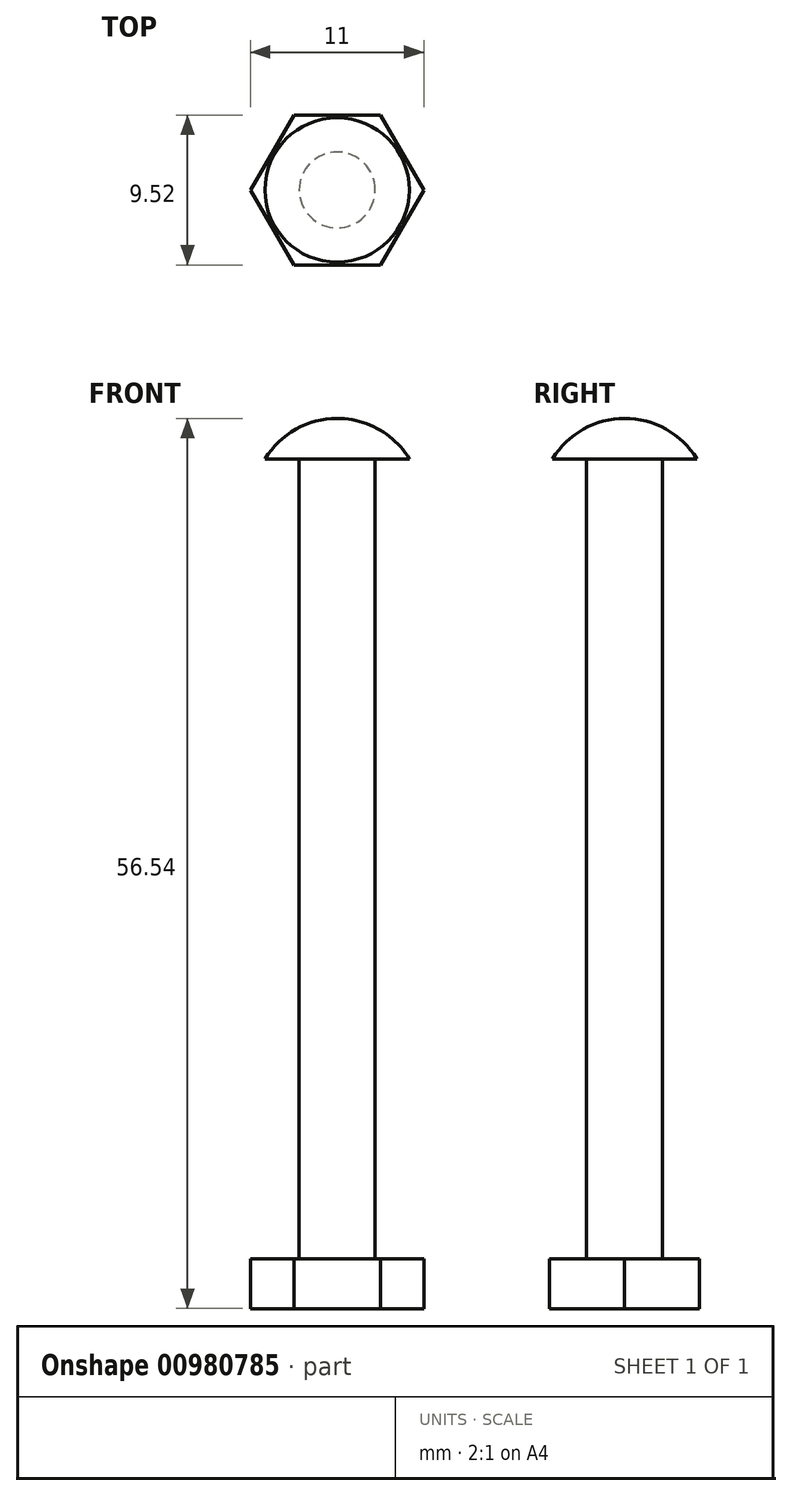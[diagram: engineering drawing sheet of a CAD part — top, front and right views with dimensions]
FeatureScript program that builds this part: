
annotation { "Feature Type Name" : "Feature", "Feature Type Description" : "" }
export const myFeature = defineFeature(function(context is Context, id is Id, definition is map)
    precondition{}
    {
        {
            var Q0;
            Q0=qCreatedBy(makeId("Front.planeOp"),FACE);
            var sketch = newSketch(context, id + "F0", { "sketchPlane" : qUnion([Q0])});
            skLineSegment(sketch, "E0", {"start": v(0, 50.8) * mm, "end": v(0, 0) * mm});
            skLineSegment(sketch, "E1", {"start": v(0, 0) * mm, "end": v(-2.41, 0) * mm});
            skLineSegment(sketch, "E2", {"start": v(-2.41, 0) * mm, "end": v(-2.41, 50.8) * mm});
            skLineSegment(sketch, "E3", {"start": v(-2.41, 50.8) * mm, "end": v(-4.58, 50.8) * mm});
            skArc(sketch, "E4", {"start": v(0, 53.37) * mm, "mid": v(-2.63, 52.68) * mm, "end": v(-4.58, 50.8) * mm});
            skLineSegment(sketch, "E5", {"start": v(0, 53.37) * mm, "end": v(4.27, 53.37) * mm, "construction": true});
            skLineSegment(sketch, "E6", {"start": v(0, 53.37) * mm, "end": v(0, 50.8) * mm});
            skSolve(sketch);
        }
        {
            var Q0;
            Q0 = qSketchRegion(id + "F0", true);
            var Q1;
            Q1=sQuery(id+"F0.wireOp",EDGE,"E0");
            revolve(context, id + "F1", {"surfaceOperationType" : NewSurfaceOperationType.NEW, "entities" : qUnion([Q0]), "axis" : qUnion([Q1]), "revolveType" : RevolveType.FULL});
        }
        {
            var Q0;
            Q0=makeQuery(id+"F1.opRevolve","SWEPT_FACE",FACE,{"disambiguationData":[OSD([sQuery(id+"F0.wireOp",EDGE,"E1")])]});
            var sketch = newSketch(context, id + "F2", { "sketchPlane" : qUnion([Q0])});
            skCircle(sketch, "E7.cCircle", {"center": v(0, 0) * mm, "radius": 4.76 * mm, "construction": true});
            skLineSegment(sketch, "E7.0", {"start": v(-2.75, 4.76) * mm, "end": v(2.75, 4.76) * mm});
            skLineSegment(sketch, "E7.1", {"start": v(2.75, 4.76) * mm, "end": v(5.5, 0) * mm});
            skLineSegment(sketch, "E7.2", {"start": v(5.5, 0) * mm, "end": v(2.75, -4.76) * mm});
            skLineSegment(sketch, "E7.3", {"start": v(2.75, -4.76) * mm, "end": v(-2.75, -4.76) * mm});
            skLineSegment(sketch, "E7.4", {"start": v(-2.75, -4.76) * mm, "end": v(-5.5, 0) * mm});
            skLineSegment(sketch, "E7.5", {"start": v(-5.5, 0) * mm, "end": v(-2.75, 4.76) * mm});
            skPoint(sketch, "E7.0.midPoint", {"position": v(0, 4.76) * mm});
            skSolve(sketch);
        }
        {
            var Q0;
            Q0 = qSketchRegion(id + "F2", true);
            extrude(context, id + "F3", {"entities" : qUnion([Q0]), "operationType" : NewBodyOperationType.ADD, "depth" : 3.17 * mm, "offsetDistance" : 25.4 * mm});
        }
    });
